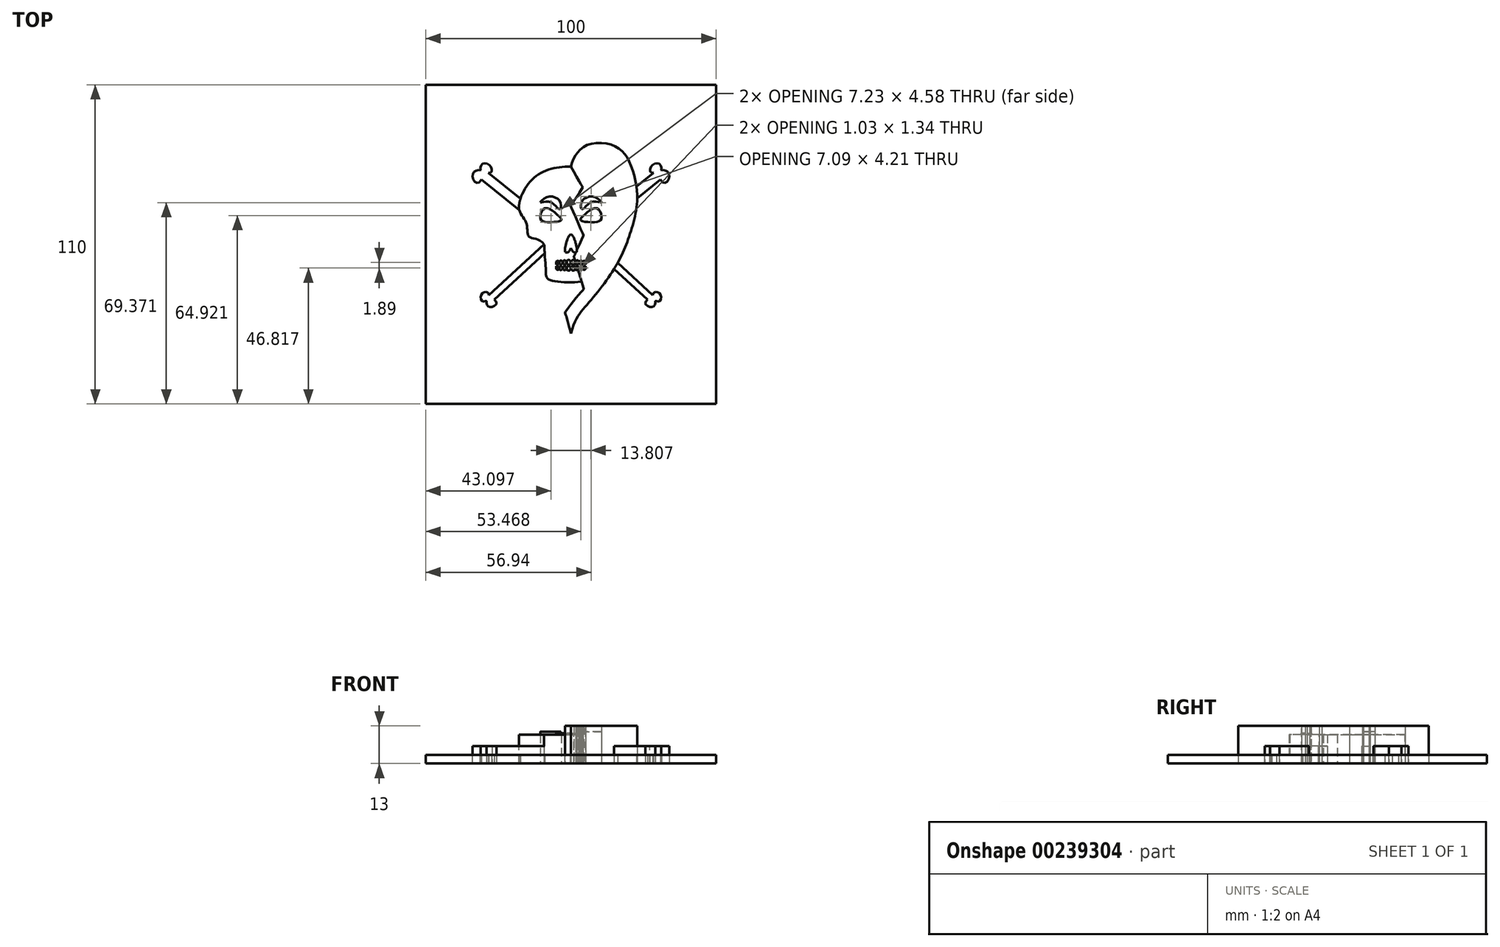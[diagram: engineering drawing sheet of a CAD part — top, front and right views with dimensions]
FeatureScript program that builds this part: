
annotation { "Feature Type Name" : "Feature", "Feature Type Description" : "" }
export const myFeature = defineFeature(function(context is Context, id is Id, definition is map)
    precondition{}
    {
        {
            var Q0;
            Q0=qCreatedBy(makeId("Top.planeOp"),FACE);
            var sketch = newSketch(context, id + "F0", { "sketchPlane" : qUnion([Q0])});
            skLineSegment(sketch, "E0.bottom", {"start": v(50, 55) * mm, "end": v(-50, 55) * mm});
            skLineSegment(sketch, "E0.top", {"start": v(50, -55) * mm, "end": v(-50, -55) * mm});
            skLineSegment(sketch, "E0.left", {"start": v(50, 55) * mm, "end": v(50, -55) * mm});
            skLineSegment(sketch, "E0.right", {"start": v(-50, 55) * mm, "end": v(-50, -55) * mm});
            skPoint(sketch, "E0.middle", {"position": v(0, 0) * mm});
            skFitSpline(sketch, "E1", {"points": [v(-4.8, 10.32) * mm, v(-9.15, 12.38) * mm, v(-10.49, 8.87) * mm, v(-8.18, 7.66) * mm, v(-3.34, 8.38) * mm, v(-4.8, 10.32) * mm]});
            skFitSpline(sketch, "E2.MirrorC", {"points": [v(4.8, 10.32) * mm, v(9.15, 12.38) * mm, v(10.49, 8.87) * mm, v(8.18, 7.66) * mm, v(3.34, 8.38) * mm, v(4.8, 10.32) * mm]});
            skFitSpline(sketch, "E3", {"points": [v(-10.49, 14.44) * mm, v(-7.34, 14.68) * mm, v(-3.94, 12.14) * mm, v(-3.58, 14.44) * mm, v(-7.94, 16.38) * mm, v(-10.49, 14.44) * mm]});
            skFitSpline(sketch, "E4.MirrorC", {"points": [v(10.49, 14.44) * mm, v(7.34, 14.68) * mm, v(3.94, 12.14) * mm, v(3.58, 14.44) * mm, v(7.94, 16.38) * mm, v(10.49, 14.44) * mm]});
            skFitSpline(sketch, "E5", {"points": [v(0, -1.3) * mm, v(-0.67, -2.5) * mm, v(-1.83, -2.7) * mm, v(-2.02, -1.44) * mm, v(-1.03, 2.2) * mm, v(0, 3.54) * mm], "startDerivative": vector(-5.03, -5.69) * mm, "endDerivative": vector(7.3, 5.01) * mm});
            skFitSpline(sketch, "E6.MirrorCS", {"points": [v(0, -1.3) * mm, v(0.67, -2.5) * mm, v(1.83, -2.7) * mm, v(2.02, -1.44) * mm, v(1.03, 2.2) * mm, v(0, 3.54) * mm], "startDerivative": vector(5.03, -5.69) * mm, "endDerivative": vector(-7.3, 5.01) * mm});
            skFitSpline(sketch, "E7", {"points": [v(-9.22, 0) * mm, v(-14.5, 2.71) * mm, v(-15.3, 7.25) * mm, v(-17.8, 11.81) * mm, v(-13.07, 22.6) * mm, v(0, 26.83) * mm], "startDerivative": vector(-29.86, 41.92) * mm, "endDerivative": vector(55.7, -0.1) * mm});
            skFitSpline(sketch, "E8.MirrorCS", {"points": [v(9.22, 0) * mm, v(14.5, 2.71) * mm, v(15.3, 7.25) * mm, v(17.8, 11.81) * mm, v(13.07, 22.6) * mm, v(0, 26.83) * mm], "startDerivative": vector(29.86, 41.92) * mm, "endDerivative": vector(-55.7, -0.1) * mm});
            skFitSpline(sketch, "E9", {"points": [v(-0.18, -6.96) * mm, v(-0.25, -5.66) * mm, v(-0.74, -5.4) * mm, v(-1.33, -5.64) * mm, v(-1.42, -6.96) * mm], "startDerivative": vector(0.08, 6.22) * mm, "endDerivative": vector(0.13, -6.29) * mm});
            skFitSpline(sketch, "E10", {"points": [v(-1.66, -6.96) * mm, v(-1.69, -5.83) * mm, v(-2.18, -5.52) * mm, v(-2.66, -5.78) * mm, v(-2.68, -6.96) * mm], "startDerivative": vector(0.09, 6.14) * mm, "endDerivative": vector(0.17, -6.74) * mm});
            skFitSpline(sketch, "E11", {"points": [v(-3, -6.96) * mm, v(-3.02, -5.85) * mm, v(-3.44, -5.62) * mm, v(-3.9, -5.82) * mm, v(-3.95, -6.96) * mm], "startDerivative": vector(0.41, 6.1) * mm, "endDerivative": vector(0.16, -5.53) * mm});
            skFitSpline(sketch, "E12", {"points": [v(-4.17, -6.96) * mm, v(-4.2, -5.89) * mm, v(-4.62, -5.7) * mm, v(-5.01, -5.91) * mm, v(-5.1, -6.96) * mm], "startDerivative": vector(0.12, 5.1) * mm, "endDerivative": vector(0.03, -4.9) * mm});
            skFitSpline(sketch, "E13.MirrorCS", {"points": [v(0.18, -6.96) * mm, v(0.25, -5.66) * mm, v(0.74, -5.4) * mm, v(1.33, -5.64) * mm, v(1.42, -6.96) * mm], "startDerivative": vector(-0.08, 6.22) * mm, "endDerivative": vector(-0.13, -6.29) * mm});
            skFitSpline(sketch, "E14.MirrorCS", {"points": [v(1.66, -6.96) * mm, v(1.69, -5.83) * mm, v(2.18, -5.52) * mm, v(2.66, -5.78) * mm, v(2.68, -6.96) * mm], "startDerivative": vector(-0.09, 6.14) * mm, "endDerivative": vector(-0.17, -6.74) * mm});
            skFitSpline(sketch, "E15.MirrorCS", {"points": [v(3, -6.96) * mm, v(3.02, -5.85) * mm, v(3.44, -5.62) * mm, v(3.9, -5.82) * mm, v(3.95, -6.96) * mm], "startDerivative": vector(-0.41, 6.1) * mm, "endDerivative": vector(-0.16, -5.53) * mm});
            skFitSpline(sketch, "E16.MirrorCS", {"points": [v(4.17, -6.96) * mm, v(4.2, -5.89) * mm, v(4.62, -5.7) * mm, v(5.01, -5.91) * mm, v(5.1, -6.96) * mm], "startDerivative": vector(-0.12, 5.1) * mm, "endDerivative": vector(-0.03, -4.9) * mm});
            skFitSpline(sketch, "E17.MirrorCS", {"points": [v(-4.17, -7.51) * mm, v(-4.2, -8.59) * mm, v(-4.62, -8.78) * mm, v(-5.01, -8.56) * mm, v(-5.1, -7.51) * mm], "startDerivative": vector(0.12, -5.1) * mm, "endDerivative": vector(0.03, 4.9) * mm});
            skFitSpline(sketch, "E18.MirrorCS", {"points": [v(-3, -7.51) * mm, v(-3.02, -8.62) * mm, v(-3.44, -8.85) * mm, v(-3.9, -8.66) * mm, v(-3.95, -7.51) * mm], "startDerivative": vector(0.41, -6.1) * mm, "endDerivative": vector(0.16, 5.53) * mm});
            skFitSpline(sketch, "E19.MirrorCS", {"points": [v(-1.66, -7.51) * mm, v(-1.69, -8.65) * mm, v(-2.18, -8.96) * mm, v(-2.66, -8.7) * mm, v(-2.68, -7.51) * mm], "startDerivative": vector(0.09, -6.14) * mm, "endDerivative": vector(0.17, 6.74) * mm});
            skFitSpline(sketch, "E20.MirrorCS", {"points": [v(-0.18, -7.51) * mm, v(-0.25, -8.82) * mm, v(-0.74, -9.07) * mm, v(-1.33, -8.84) * mm, v(-1.42, -7.51) * mm], "startDerivative": vector(0.08, -6.22) * mm, "endDerivative": vector(0.13, 6.29) * mm});
            skFitSpline(sketch, "E21.MirrorCS", {"points": [v(0.18, -7.51) * mm, v(0.25, -8.82) * mm, v(0.74, -9.07) * mm, v(1.33, -8.84) * mm, v(1.42, -7.51) * mm], "startDerivative": vector(-0.08, -6.22) * mm, "endDerivative": vector(-0.13, 6.29) * mm});
            skFitSpline(sketch, "E22.MirrorCS", {"points": [v(1.66, -7.51) * mm, v(1.69, -8.65) * mm, v(2.18, -8.96) * mm, v(2.66, -8.7) * mm, v(2.68, -7.51) * mm], "startDerivative": vector(-0.09, -6.14) * mm, "endDerivative": vector(-0.17, 6.74) * mm});
            skFitSpline(sketch, "E23.MirrorCS", {"points": [v(3, -7.51) * mm, v(3.02, -8.62) * mm, v(3.44, -8.85) * mm, v(3.9, -8.66) * mm, v(3.95, -7.51) * mm], "startDerivative": vector(-0.41, -6.1) * mm, "endDerivative": vector(-0.16, 5.53) * mm});
            skFitSpline(sketch, "E24.MirrorCS", {"points": [v(4.17, -7.51) * mm, v(4.2, -8.59) * mm, v(4.62, -8.78) * mm, v(5.01, -8.56) * mm, v(5.1, -7.51) * mm], "startDerivative": vector(-0.12, -5.1) * mm, "endDerivative": vector(-0.03, 4.9) * mm});
            skLineSegment(sketch, "E25", {"start": v(-5.1, -6.96) * mm, "end": v(-4.17, -6.96) * mm});
            skLineSegment(sketch, "E26", {"start": v(-3.95, -6.96) * mm, "end": v(-3, -6.96) * mm});
            skLineSegment(sketch, "E27", {"start": v(-2.68, -6.96) * mm, "end": v(-1.66, -6.96) * mm});
            skLineSegment(sketch, "E28", {"start": v(-1.42, -6.96) * mm, "end": v(-0.18, -6.96) * mm});
            skLineSegment(sketch, "E29", {"start": v(0.18, -6.96) * mm, "end": v(1.42, -6.96) * mm});
            skLineSegment(sketch, "E30", {"start": v(1.66, -6.96) * mm, "end": v(2.68, -6.96) * mm});
            skLineSegment(sketch, "E31", {"start": v(3, -6.96) * mm, "end": v(3.95, -6.96) * mm});
            skLineSegment(sketch, "E32", {"start": v(4.17, -6.96) * mm, "end": v(5.1, -6.96) * mm});
            skLineSegment(sketch, "E33", {"start": v(-5.1, -7.51) * mm, "end": v(-4.17, -7.51) * mm});
            skLineSegment(sketch, "E34", {"start": v(-3.95, -7.51) * mm, "end": v(-3, -7.51) * mm});
            skLineSegment(sketch, "E35", {"start": v(-2.68, -7.51) * mm, "end": v(-1.66, -7.51) * mm});
            skLineSegment(sketch, "E36", {"start": v(-1.42, -7.51) * mm, "end": v(-0.18, -7.51) * mm});
            skLineSegment(sketch, "E37", {"start": v(0.18, -7.51) * mm, "end": v(1.42, -7.51) * mm});
            skLineSegment(sketch, "E38", {"start": v(1.66, -7.51) * mm, "end": v(2.68, -7.51) * mm});
            skLineSegment(sketch, "E39", {"start": v(3, -7.51) * mm, "end": v(3.95, -7.51) * mm});
            skLineSegment(sketch, "E40", {"start": v(4.17, -7.51) * mm, "end": v(5.1, -7.51) * mm});
            skFitSpline(sketch, "E41", {"points": [v(-9.22, 0) * mm, v(-8.61, -9.78) * mm, v(-7.97, -11.85) * mm, v(0, -13.1) * mm, v(8.12, -11.61) * mm, v(8.94, -9.47) * mm, v(9.22, 0) * mm], "startDerivative": vector(3.29, -60.32) * mm, "endDerivative": vector(0.99, 66.41) * mm});
            skFitSpline(sketch, "E42", {"points": [v(0, 26.83) * mm, v(1.93, 31.24) * mm, v(6.04, 34.44) * mm, v(13.58, 34.44) * mm, v(18.33, 31.42) * mm, v(21.24, 25.6) * mm, v(22.85, 15.6) * mm, v(20.6, 4.3) * mm, v(16.72, -5.25) * mm, v(11, -14.13) * mm, v(4.61, -21.96) * mm, v(0, -30.74) * mm], "startDerivative": vector(14.87, 77.4) * mm, "endDerivative": vector(-38.8, -148.07) * mm});
            skFitSpline(sketch, "E43", {"points": [v(0, 26.83) * mm, v(4, 19.8) * mm, v(4.04, 19.6) * mm, v(0, 13.46) * mm, v(0, 13.09) * mm, v(4.29, 3.24) * mm, v(4.3, 3.04) * mm, v(1.05, -4.17) * mm, v(1.07, -4.41) * mm, v(4.4, -15.3) * mm, v(4.32, -15.58) * mm, v(-1.83, -23.25) * mm, v(-1.83, -24.22) * mm, v(0, -30.74) * mm], "startDerivative": vector(44.9, -81.3) * mm, "endDerivative": vector(20.67, -80.8) * mm});
            skLineSegment(sketch, "E44", {"start": v(-9.22, 0) * mm, "end": v(-28.25, -17.47) * mm});
            skLineSegment(sketch, "E45", {"start": v(-9.04, -3.1) * mm, "end": v(-26.48, -19.1) * mm});
            skFitSpline(sketch, "E46", {"points": [v(-28.25, -17.47) * mm, v(-28.55, -16.7) * mm, v(-29.74, -16.47) * mm, v(-31, -17.7) * mm, v(-30.61, -19.58) * mm, v(-29.39, -19.58) * mm, v(-29.06, -19.52) * mm, v(-29.06, -19.82) * mm, v(-28.76, -21.1) * mm, v(-27.05, -21.53) * mm, v(-25.67, -20.33) * mm, v(-26.48, -19.1) * mm], "startDerivative": vector(-1.76, 11.33) * mm, "endDerivative": vector(-12.64, 11.76) * mm});
            skLineSegment(sketch, "E47.MirrorCS", {"start": v(16.13, -6.35) * mm, "end": v(28.25, -17.47) * mm});
            skLineSegment(sketch, "E48.MirrorCS", {"start": v(9.04, -3.1) * mm, "end": v(9.17, -3.21) * mm});
            skFitSpline(sketch, "E49.MirrorCS", {"points": [v(28.25, -17.47) * mm, v(28.55, -16.7) * mm, v(29.74, -16.47) * mm, v(31, -17.7) * mm, v(30.61, -19.58) * mm, v(29.39, -19.58) * mm, v(29.06, -19.52) * mm, v(29.06, -19.82) * mm, v(28.76, -21.1) * mm, v(27.05, -21.53) * mm, v(25.67, -20.33) * mm, v(26.48, -19.1) * mm], "startDerivative": vector(1.76, 11.33) * mm, "endDerivative": vector(12.64, 11.76) * mm});
            skLineSegment(sketch, "E50", {"start": v(-17.8, 11.81) * mm, "end": v(-30.85, 22.34) * mm});
            skLineSegment(sketch, "E51", {"start": v(-17.4, 15.7) * mm, "end": v(-28.44, 24.61) * mm});
            skFitSpline(sketch, "E52", {"points": [v(-28.44, 24.61) * mm, v(-27.36, 25.04) * mm, v(-27.45, 26.52) * mm, v(-28.89, 27.8) * mm, v(-30.58, 27.67) * mm, v(-31.22, 25.97) * mm, v(-31.09, 25.55) * mm, v(-31.43, 25.6) * mm, v(-33.08, 25.21) * mm, v(-33.93, 23.39) * mm, v(-32.83, 21.4) * mm, v(-31.43, 21.48) * mm, v(-30.85, 22.34) * mm], "startDerivative": vector(16.56, 2.66) * mm, "endDerivative": vector(13.2, 12.8) * mm});
            skLineSegment(sketch, "E53.MirrorCS", {"start": v(22.58, 19.88) * mm, "end": v(28.44, 24.61) * mm});
            skLineSegment(sketch, "E54.MirrorCS", {"start": v(22.86, 15.9) * mm, "end": v(30.85, 22.34) * mm});
            skFitSpline(sketch, "E55.MirrorCS", {"points": [v(28.44, 24.61) * mm, v(27.36, 25.04) * mm, v(27.45, 26.52) * mm, v(28.89, 27.8) * mm, v(30.58, 27.67) * mm, v(31.22, 25.97) * mm, v(31.09, 25.55) * mm, v(31.43, 25.6) * mm, v(33.08, 25.21) * mm, v(33.93, 23.39) * mm, v(32.83, 21.4) * mm, v(31.43, 21.48) * mm, v(30.85, 22.34) * mm], "startDerivative": vector(-16.56, 2.66) * mm, "endDerivative": vector(-13.2, 12.8) * mm});
            skPoint(sketch, "E56.orphan", {"position": v(17.4, 15.7) * mm});
            skLineSegment(sketch, "E57.trimOffspring", {"start": v(14.9, -8.47) * mm, "end": v(26.48, -19.1) * mm});
            skSolve(sketch);
        }
        {
            var Q0;
            Q0=qSketchRegion(id+"F0",true);
            extrude(context, id + "F1", {"entities" : qUnion([Q0]), "depth" : 3 * mm});
        }
        {
            var Q0;
            Q0=makeQuery(id+"F0.imprint","IMPRINT",FACE,{"disambiguationData":[TD([[makeQuery(id+"F0.imprint","IMPRINT",EDGE,{"derivedFrom":sQuery(id+"F0.wireOp",EDGE,"E1")}),-1.0]])]});
            extrude(context, id + "F2", {"entities" : qUnion([Q0]), "operationType" : NewBodyOperationType.ADD, "depth" : 10 * mm});
        }
        {
            var Q0;
            Q0=makeQuery(id+"F0.imprint","IMPRINT",FACE,{"disambiguationData":[TD([[makeQuery(id+"F0.imprint","IMPRINT",EDGE,{"derivedFrom":sQuery(id+"F0.wireOp",EDGE,"E12")}),1.0]])]});
            var Q1;
            Q1=makeQuery(id+"F0.imprint","IMPRINT",FACE,{"disambiguationData":[TD([[makeQuery(id+"F0.imprint","IMPRINT",EDGE,{"derivedFrom":sQuery(id+"F0.wireOp",EDGE,"E11")}),1.0]])]});
            var Q2;
            Q2=makeQuery(id+"F0.imprint","IMPRINT",FACE,{"disambiguationData":[TD([[makeQuery(id+"F0.imprint","IMPRINT",EDGE,{"derivedFrom":sQuery(id+"F0.wireOp",EDGE,"E10")}),1.0]])]});
            var Q3;
            Q3=makeQuery(id+"F0.imprint","IMPRINT",FACE,{"disambiguationData":[TD([[makeQuery(id+"F0.imprint","IMPRINT",EDGE,{"derivedFrom":sQuery(id+"F0.wireOp",EDGE,"E9")}),1.0]])]});
            var Q4;
            Q4=makeQuery(id+"F0.imprint","IMPRINT",FACE,{"disambiguationData":[TD([[makeQuery(id+"F0.imprint","IMPRINT",EDGE,{"derivedFrom":sQuery(id+"F0.wireOp",EDGE,"E13.MirrorCS")}),-1.0]])]});
            var Q5;
            Q5=makeQuery(id+"F0.imprint","IMPRINT",FACE,{"disambiguationData":[TD([[makeQuery(id+"F0.imprint","IMPRINT",EDGE,{"derivedFrom":sQuery(id+"F0.wireOp",EDGE,"E14.MirrorCS")}),-1.0]])]});
            var Q6;
            Q6=makeQuery(id+"F0.imprint","IMPRINT",FACE,{"disambiguationData":[TD([[makeQuery(id+"F0.imprint","IMPRINT",EDGE,{"derivedFrom":sQuery(id+"F0.wireOp",EDGE,"E15.MirrorCS")}),-1.0]])]});
            var Q7;
            Q7=makeQuery(id+"F0.imprint","IMPRINT",FACE,{"disambiguationData":[TD([[makeQuery(id+"F0.imprint","IMPRINT",EDGE,{"derivedFrom":sQuery(id+"F0.wireOp",EDGE,"E16.MirrorCS")}),-1.0]])]});
            var Q8;
            Q8=makeQuery(id+"F0.imprint","IMPRINT",FACE,{"disambiguationData":[TD([[makeQuery(id+"F0.imprint","IMPRINT",EDGE,{"derivedFrom":sQuery(id+"F0.wireOp",EDGE,"E24.MirrorCS")}),1.0]])]});
            var Q9;
            Q9=makeQuery(id+"F0.imprint","IMPRINT",FACE,{"disambiguationData":[TD([[makeQuery(id+"F0.imprint","IMPRINT",EDGE,{"derivedFrom":sQuery(id+"F0.wireOp",EDGE,"E23.MirrorCS")}),1.0]])]});
            var Q10;
            Q10=makeQuery(id+"F0.imprint","IMPRINT",FACE,{"disambiguationData":[TD([[makeQuery(id+"F0.imprint","IMPRINT",EDGE,{"derivedFrom":sQuery(id+"F0.wireOp",EDGE,"E22.MirrorCS")}),1.0]])]});
            var Q11;
            Q11=makeQuery(id+"F0.imprint","IMPRINT",FACE,{"disambiguationData":[TD([[makeQuery(id+"F0.imprint","IMPRINT",EDGE,{"derivedFrom":sQuery(id+"F0.wireOp",EDGE,"E21.MirrorCS")}),1.0]])]});
            var Q12;
            Q12=makeQuery(id+"F0.imprint","IMPRINT",FACE,{"disambiguationData":[TD([[makeQuery(id+"F0.imprint","IMPRINT",EDGE,{"derivedFrom":sQuery(id+"F0.wireOp",EDGE,"E20.MirrorCS")}),-1.0]])]});
            var Q13;
            Q13=makeQuery(id+"F0.imprint","IMPRINT",FACE,{"disambiguationData":[TD([[makeQuery(id+"F0.imprint","IMPRINT",EDGE,{"derivedFrom":sQuery(id+"F0.wireOp",EDGE,"E19.MirrorCS")}),-1.0]])]});
            var Q14;
            Q14=makeQuery(id+"F0.imprint","IMPRINT",FACE,{"disambiguationData":[TD([[makeQuery(id+"F0.imprint","IMPRINT",EDGE,{"derivedFrom":sQuery(id+"F0.wireOp",EDGE,"E18.MirrorCS")}),-1.0]])]});
            var Q15;
            Q15=makeQuery(id+"F0.imprint","IMPRINT",FACE,{"disambiguationData":[TD([[makeQuery(id+"F0.imprint","IMPRINT",EDGE,{"derivedFrom":sQuery(id+"F0.wireOp",EDGE,"E17.MirrorCS")}),-1.0]])]});
            extrude(context, id + "F3", {"entities" : qUnion([Q0, Q1, Q2, Q3, Q4, Q5, Q6, Q7, Q8, Q9, Q10, Q11, Q12, Q13, Q14, Q15]), "operationType" : NewBodyOperationType.ADD, "depth" : 10.5 * mm});
        }
        {
            var Q0;
            Q0=makeQuery(id+"F0.imprint","IMPRINT",FACE,{"disambiguationData":[TD([[makeQuery(id+"F0.imprint","IMPRINT",EDGE,{"derivedFrom":sQuery(id+"F0.wireOp",EDGE,"E3")}),1.0]])]});
            var Q1;
            Q1=makeQuery(id+"F0.imprint","IMPRINT",FACE,{"disambiguationData":[TD([[makeQuery(id+"F0.imprint","IMPRINT",EDGE,{"derivedFrom":sQuery(id+"F0.wireOp",EDGE,"E4.MirrorC")}),-1.0]])]});
            extrude(context, id + "F4", {"entities" : qUnion([Q0, Q1]), "operationType" : NewBodyOperationType.ADD, "depth" : 11 * mm});
        }
        {
            var Q0;
            {var subQ0=sQuery(id+"F0.wireOp",EDGE,"E8.MirrorCS");Q0=makeQuery(id+"F0.imprint","IMPRINT",FACE,{"disambiguationData":[TD([[makeQuery(id+"F0.imprint","IMPRINT",EDGE,{"derivedFrom":subQ0}),-1.0]])]});}
            var Q1;
            Q1=makeQuery(id+"F0.imprint","IMPRINT",FACE,{"disambiguationData":[TD([[makeQuery(id+"F0.imprint","IMPRINT",EDGE,{"derivedFrom":sQuery(id+"F0.wireOp",EDGE,"E2.MirrorC")}),1.0]])]});
            extrude(context, id + "F5", {"entities" : qUnion([Q0, Q1]), "depth" : 13 * mm});
        }
        {
            var Q0;
            {var subQ0=sQuery(id+"F0.wireOp",EDGE,"E50");Q0=makeQuery(id+"F0.imprint","IMPRINT",FACE,{"disambiguationData":[TD([[makeQuery(id+"F0.imprint","IMPRINT",EDGE,{"derivedFrom":subQ0}),-1.0]])]});}
            var Q1;
            {var subQ0=sQuery(id+"F0.wireOp",EDGE,"E53.MirrorCS");Q1=makeQuery(id+"F0.imprint","IMPRINT",FACE,{"disambiguationData":[TD([[makeQuery(id+"F0.imprint","IMPRINT",EDGE,{"derivedFrom":subQ0}),-1.0]])]});}
            var Q2;
            {var subQ0=sQuery(id+"F0.wireOp",EDGE,"E47.MirrorCS");Q2=makeQuery(id+"F0.imprint","IMPRINT",FACE,{"disambiguationData":[TD([[makeQuery(id+"F0.imprint","IMPRINT",EDGE,{"derivedFrom":subQ0}),-1.0]])]});}
            var Q3;
            {var subQ0=sQuery(id+"F0.wireOp",EDGE,"E44");Q3=makeQuery(id+"F0.imprint","IMPRINT",FACE,{"disambiguationData":[TD([[makeQuery(id+"F0.imprint","IMPRINT",EDGE,{"derivedFrom":subQ0}),1.0]])]});}
            extrude(context, id + "F6", {"entities" : qUnion([Q0, Q1, Q2, Q3]), "depth" : 6 * mm});
        }
    });
